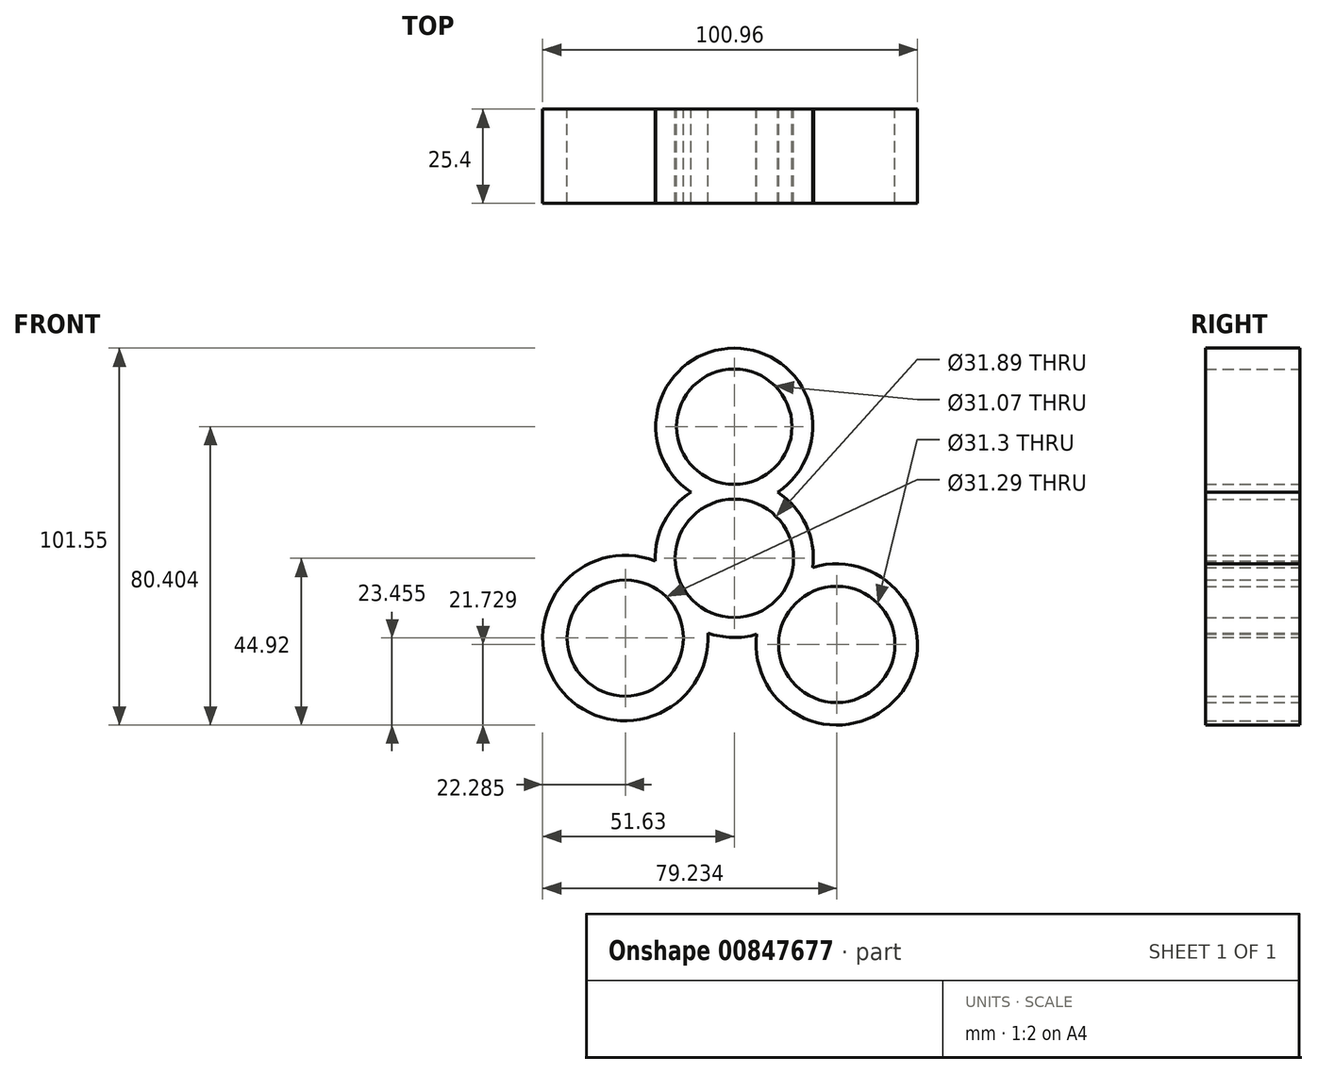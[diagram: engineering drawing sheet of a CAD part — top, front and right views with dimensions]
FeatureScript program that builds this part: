
annotation { "Feature Type Name" : "Feature", "Feature Type Description" : "" }
export const myFeature = defineFeature(function(context is Context, id is Id, definition is map)
    precondition{}
    {
        {
            var Q0;
            Q0=qCreatedBy(makeId("Front.planeOp"),FACE);
            var sketch = newSketch(context, id + "F0", { "sketchPlane" : qUnion([Q0])});
            skArc(sketch, "E0", {"start": v(-11.67, 17.85) * mm, "mid": v(-18.91, 9.85) * mm, "end": v(-21.31, -0.68) * mm});
            skCircle(sketch, "E1", {"center": v(0, 0) * mm, "radius": 15.95 * mm});
            skCircle(sketch, "E2", {"center": v(0, 35.48) * mm, "radius": 15.53 * mm});
            skArc(sketch, "E3", {"start": v(11.67, 17.85) * mm, "mid": v(0, 56.63) * mm, "end": v(-11.67, 17.85) * mm});
            skCircle(sketch, "E4", {"center": v(27.6, -23.2) * mm, "radius": 15.65 * mm});
            skArc(sketch, "E5", {"start": v(6.05, -20.45) * mm, "mid": v(44.24, -37.17) * mm, "end": v(21.18, -2.43) * mm});
            skCircle(sketch, "E6", {"center": v(-29.34, -21.47) * mm, "radius": 15.64 * mm});
            skArc(sketch, "E7", {"start": v(-21.31, -0.68) * mm, "mid": v(-47.33, -34.62) * mm, "end": v(-7.1, -20.1) * mm});
            skArc(sketch, "E8.trimOffspring", {"start": v(-7.1, -20.1) * mm, "mid": v(-0.55, -21.32) * mm, "end": v(6.05, -20.45) * mm});
            skArc(sketch, "E9.trimOffspring", {"start": v(21.18, -2.43) * mm, "mid": v(19.3, 9.06) * mm, "end": v(11.67, 17.85) * mm});
            skSolve(sketch);
        }
        {
            var Q0;
            Q0 = qSketchRegion(id + "F0", true);
            extrude(context, id + "F1", {"entities" : qUnion([Q0]), "depth" : 25.4 * mm, "offsetDistance" : 25.4 * mm});
        }
    });
